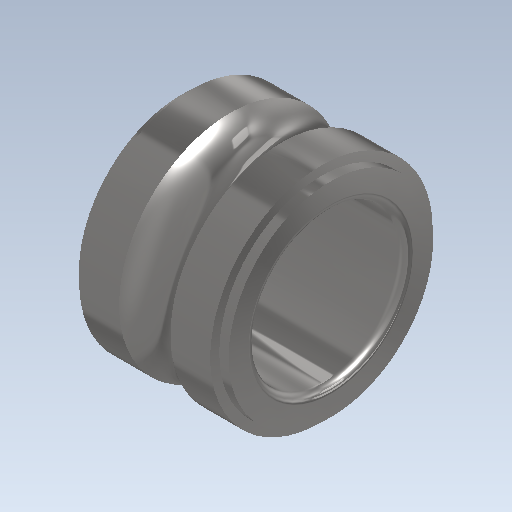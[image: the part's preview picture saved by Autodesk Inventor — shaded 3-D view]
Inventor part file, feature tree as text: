
AUTODESK INVENTOR PART (.ipt)
format: ipt  version: 2020.3 (Build 243373000, 373)  size: 208,896 bytes
history: native  units: mm (DEFAULTED — no unit token found)
features: other x70, revolve x1, sketch x1
ambient origin geometry x8: Origin, YZ Plane, XZ Plane, XY Plane, X Axis, Y Axis, Z Axis, Center Point
bodies: Solid1 (feature_tree)
feature tree (72):
  revolve  "Revolution1"  [1 undecoded]
  other  "ip_st_1_1_XY"
  other  "ip_st_1_1_YZ"
  other  "ip_st_1_1_ZX"
  other  "ip_st_1_1_X"
  other  "ip_st_1_1_Y"
  other  "ip_st_1_1_Z"
  other  "ip_st_1_1_Center"
  other  "ip_st_1_2_XY"
  other  "ip_st_1_2_YZ"
  other  "ip_st_1_2_ZX"
  other  "ip_st_1_2_X"
  other  "ip_st_1_2_Y"
  other  "ip_st_1_2_Z"
  other  "ip_st_1_2_Center"
  other  "ip_st_1_3_XY"
  other  "ip_st_1_3_YZ"
  other  "ip_st_1_3_ZX"
  other  "ip_st_1_3_X"
  other  "ip_st_1_3_Y"
  other  "ip_st_1_3_Z"
  other  "ip_st_1_3_Center"
  other  "ip_st_1_4_XY"
  other  "ip_st_1_4_YZ"
  other  "ip_st_1_4_ZX"
  other  "ip_st_1_4_X"
  other  "ip_st_1_4_Y"
  other  "ip_st_1_4_Z"
  other  "ip_st_1_4_Center"
  other  "ip_st_1_5_XY"
  other  "ip_st_1_5_YZ"
  other  "ip_st_1_5_ZX"
  other  "ip_st_1_5_X"
  other  "ip_st_1_5_Y"
  other  "ip_st_1_5_Z"
  other  "ip_st_1_5_Center"
  other  "ip_st_1_6_XY"
  other  "ip_st_1_6_YZ"
  other  "ip_st_1_6_ZX"
  other  "ip_st_1_6_X"
  other  "ip_st_1_6_Y"
  other  "ip_st_1_6_Z"
  other  "ip_st_1_6_Center"
  other  "ip_st_1_7_XY"
  other  "ip_st_1_7_YZ"
  other  "ip_st_1_7_ZX"
  other  "ip_st_1_7_X"
  other  "ip_st_1_7_Y"
  other  "ip_st_1_7_Z"
  other  "ip_st_1_7_Center"
  other  "ip_st_1_8_XY"
  other  "ip_st_1_8_YZ"
  other  "ip_st_1_8_ZX"
  other  "ip_st_1_8_X"
  other  "ip_st_1_8_Y"
  other  "ip_st_1_8_Z"
  other  "ip_st_1_8_Center"
  other  "ip_st_1a_XY"
  other  "ip_st_1a_YZ"
  other  "ip_st_1a_ZX"
  other  "ip_st_1a_X"
  other  "ip_st_1a_Y"
  other  "ip_st_1a_Z"
  other  "ip_st_1a_Center"
  other  "ip_st_2a_XY"
  other  "ip_st_2a_YZ"
  other  "ip_st_2a_ZX"
  other  "ip_st_2a_X"
  other  "ip_st_2a_Y"
  other  "ip_st_2a_Z"
  other  "ip_st_2a_Center"
  sketch  "Sketch_2"  dims[d0=360.0deg d1=0.0mm d2=0.0mm]
note: 1 required parameter value undecoded (feature->parameter linkage not recoverable at this tier; creation-order binding heuristic only, values carry confidence <= 0.55)
